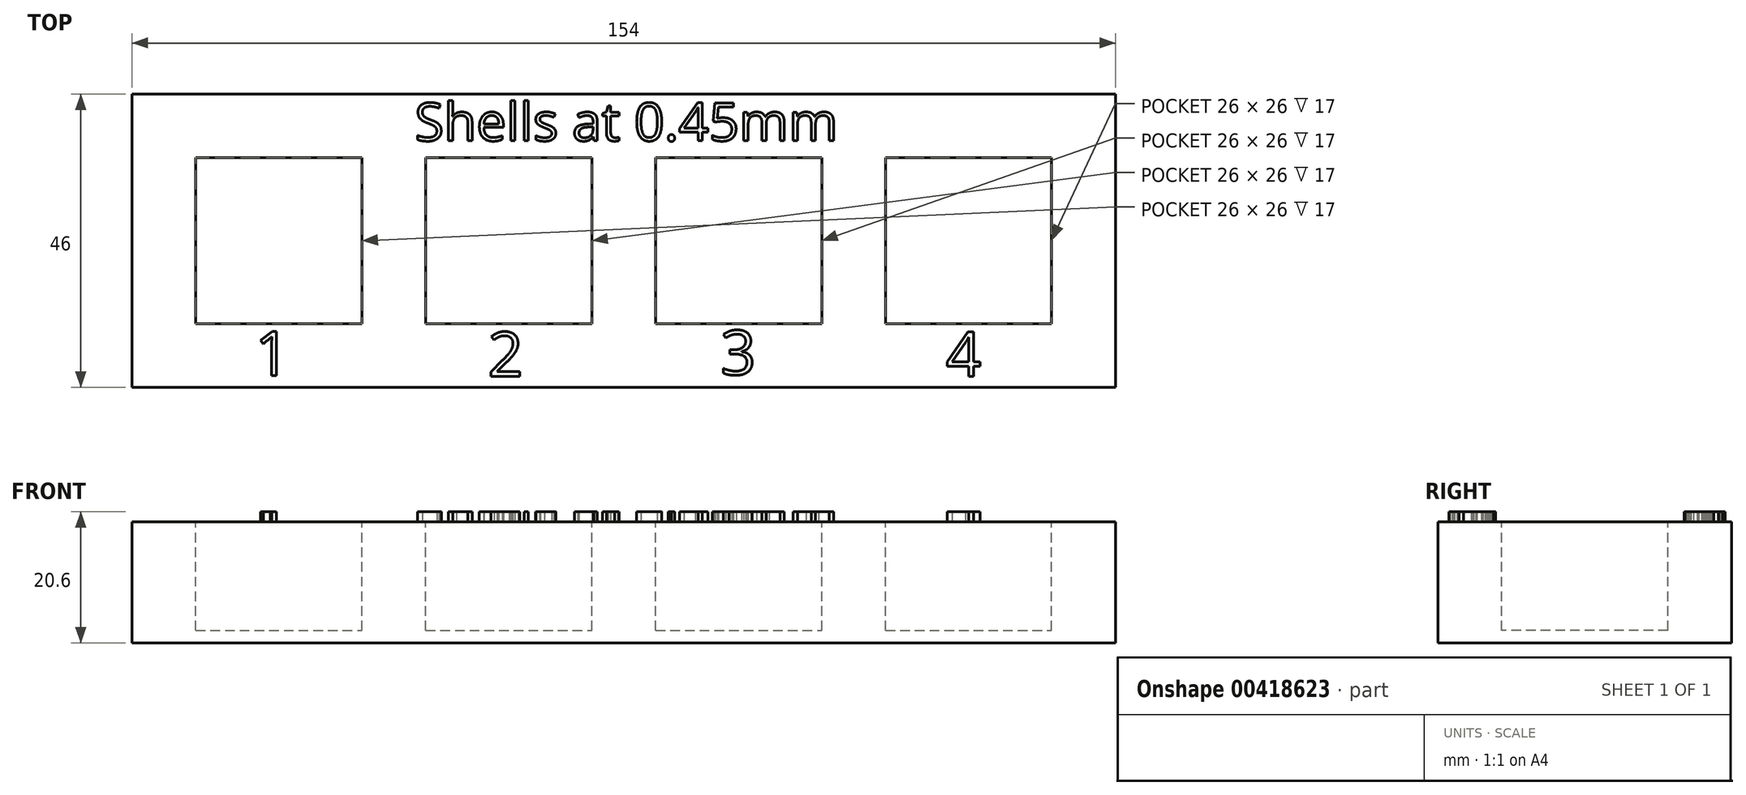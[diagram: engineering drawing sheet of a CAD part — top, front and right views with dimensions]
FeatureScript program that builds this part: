
annotation { "Feature Type Name" : "Feature", "Feature Type Description" : "" }
export const myFeature = defineFeature(function(context is Context, id is Id, definition is map)
    precondition{}
    {
        {
            var Q0;
            Q0=qCreatedBy(makeId("Top.planeOp"),FACE);
            var sketch = newSketch(context, id + "F0", { "sketchPlane" : qUnion([Q0])});
            skLineSegment(sketch, "E0.bottom", {"start": v(0, 0) * mm, "end": v(-154, 0) * mm});
            skLineSegment(sketch, "E0.top", {"start": v(0, 46) * mm, "end": v(-154, 46) * mm});
            skLineSegment(sketch, "E0.left", {"start": v(0, 0) * mm, "end": v(0, 46) * mm});
            skLineSegment(sketch, "E0.right", {"start": v(-154, 0) * mm, "end": v(-154, 46) * mm});
            skLineSegment(sketch, "E1.bottom", {"start": v(-144, 36) * mm, "end": v(-118, 36) * mm});
            skLineSegment(sketch, "E1.top", {"start": v(-144, 10) * mm, "end": v(-118, 10) * mm});
            skLineSegment(sketch, "E1.left", {"start": v(-144, 36) * mm, "end": v(-144, 10) * mm});
            skLineSegment(sketch, "E1.right", {"start": v(-118, 36) * mm, "end": v(-118, 10) * mm});
            skLineSegment(sketch, "E2.bottom", {"start": v(-108, 36) * mm, "end": v(-82, 36) * mm});
            skLineSegment(sketch, "E2.top", {"start": v(-108, 10) * mm, "end": v(-82, 10) * mm});
            skLineSegment(sketch, "E2.left", {"start": v(-108, 36) * mm, "end": v(-108, 10) * mm});
            skLineSegment(sketch, "E2.right", {"start": v(-82, 36) * mm, "end": v(-82, 10) * mm});
            skLineSegment(sketch, "E3.bottom", {"start": v(-72, 36) * mm, "end": v(-46, 36) * mm});
            skLineSegment(sketch, "E3.top", {"start": v(-72, 10) * mm, "end": v(-46, 10) * mm});
            skLineSegment(sketch, "E3.left", {"start": v(-72, 36) * mm, "end": v(-72, 10) * mm});
            skLineSegment(sketch, "E3.right", {"start": v(-46, 36) * mm, "end": v(-46, 10) * mm});
            skLineSegment(sketch, "E4.bottom", {"start": v(-36, 36) * mm, "end": v(-10, 36) * mm});
            skLineSegment(sketch, "E4.top", {"start": v(-36, 10) * mm, "end": v(-10, 10) * mm});
            skLineSegment(sketch, "E4.left", {"start": v(-36, 36) * mm, "end": v(-36, 10) * mm});
            skLineSegment(sketch, "E4.right", {"start": v(-10, 36) * mm, "end": v(-10, 10) * mm});
            skSolve(sketch);
        }
        {
            var Q0;
            Q0=qSketchRegion(id+"F0",true);
            var Q1;
            Q1=makeQuery(id+"F0.imprint","IMPRINT",FACE,{"disambiguationData":[TD([[makeQuery(id+"F0.imprint","IMPRINT",EDGE,{"derivedFrom":sQuery(id+"F0.wireOp",EDGE,"E1.bottom")}),-1.0]])]});
            var Q2;
            Q2=makeQuery(id+"F0.imprint","IMPRINT",FACE,{"disambiguationData":[TD([[makeQuery(id+"F0.imprint","IMPRINT",EDGE,{"derivedFrom":sQuery(id+"F0.wireOp",EDGE,"E2.bottom")}),-1.0]])]});
            var Q3;
            Q3=makeQuery(id+"F0.imprint","IMPRINT",FACE,{"disambiguationData":[TD([[makeQuery(id+"F0.imprint","IMPRINT",EDGE,{"derivedFrom":sQuery(id+"F0.wireOp",EDGE,"E3.bottom")}),-1.0]])]});
            var Q4;
            Q4=makeQuery(id+"F0.imprint","IMPRINT",FACE,{"disambiguationData":[TD([[makeQuery(id+"F0.imprint","IMPRINT",EDGE,{"derivedFrom":sQuery(id+"F0.wireOp",EDGE,"E4.bottom")}),-1.0]])]});
            extrude(context, id + "F1", {"entities" : qUnion([Q0, Q1, Q2, Q3, Q4]), "oppositeDirection" : true, "depth" : 19 * mm});
        }
        {
            var Q0;
            Q0=makeQuery(id+"F0.imprint","IMPRINT",FACE,{"disambiguationData":[TD([[makeQuery(id+"F0.imprint","IMPRINT",EDGE,{"derivedFrom":sQuery(id+"F0.wireOp",EDGE,"E1.bottom")}),-1.0]])]});
            var Q1;
            Q1=makeQuery(id+"F0.imprint","IMPRINT",FACE,{"disambiguationData":[TD([[makeQuery(id+"F0.imprint","IMPRINT",EDGE,{"derivedFrom":sQuery(id+"F0.wireOp",EDGE,"E2.bottom")}),-1.0]])]});
            var Q2;
            Q2=makeQuery(id+"F0.imprint","IMPRINT",FACE,{"disambiguationData":[TD([[makeQuery(id+"F0.imprint","IMPRINT",EDGE,{"derivedFrom":sQuery(id+"F0.wireOp",EDGE,"E3.bottom")}),-1.0]])]});
            var Q3;
            Q3=makeQuery(id+"F0.imprint","IMPRINT",FACE,{"disambiguationData":[TD([[makeQuery(id+"F0.imprint","IMPRINT",EDGE,{"derivedFrom":sQuery(id+"F0.wireOp",EDGE,"E4.bottom")}),-1.0]])]});
            extrude(context, id + "F2", {"entities" : qUnion([Q0, Q1, Q2, Q3]), "operationType" : NewBodyOperationType.REMOVE, "oppositeDirection" : true, "depth" : 17 * mm});
        }
        {
            var Q0;
            Q0=makeQuery(id+"F0.imprint","IMPRINT",FACE,{"disambiguationData":[TD([[makeQuery(id+"F0.imprint","IMPRINT",EDGE,{"derivedFrom":sQuery(id+"F0.wireOp",EDGE,"E0.bottom")}),-1.0]])]});
            var sketch = newSketch(context, id + "F3", { "sketchPlane" : qUnion([Q0])});
            skText(sketch, "E5", { "text": "Shells at 0.45mm", "fontName": "OpenSans-Regular.ttf"});
            skText(sketch, "E6", { "text": "1", "fontName": "OpenSans-Regular.ttf"});
            skText(sketch, "E7", { "text": "2", "fontName": "OpenSans-Regular.ttf"});
            skText(sketch, "E8", { "text": "3", "fontName": "OpenSans-Regular.ttf"});
            skText(sketch, "E9", { "text": "4", "fontName": "OpenSans-Regular.ttf"});
            const initialGuessF3  = {"E5": [-0.10972, 0.03865, 1, 0, 0.00598], "E6": [-0.13474, 0.00183, 1, 0, 0.007], "E7": [-0.09828, 0.00172, 1, 0, 0.007], "E8": [-0.06187, 0.00197, 1, 0, 0.007], "E9": [-0.02658, 0.0017, 1, 0, 0.007]};
            skSetInitialGuess(sketch, initialGuessF3);
            skSolve(sketch);
        }
        {
            var Q0;
            Q0=qSketchRegion(id+"F3",true);
            extrude(context, id + "F4", {"entities" : qUnion([Q0]), "operationType" : NewBodyOperationType.ADD, "depth" : 1.6 * mm});
        }
    });
